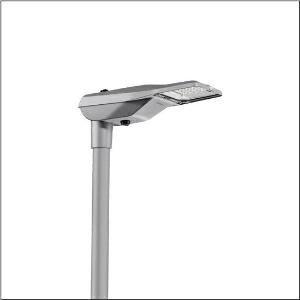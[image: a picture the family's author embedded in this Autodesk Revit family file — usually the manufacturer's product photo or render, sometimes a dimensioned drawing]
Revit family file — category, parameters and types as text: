
# Revit family: streetlight_sl_21_iq_micro___st1_0a_5xe1d21y08db_e1fc
name_source: partatom
category: Lighting Fixtures
units: mm (PartAtom-declared; Revit-internal decimal feet)

## family parameters
Cut with Voids When Loaded = No
Host = Face
Light Source = No
Part Type = Normal
Room Calculation Point = No
Round Connector Dimension = Use Diameter
Shared = No

## types (1)
- --- (1 x LED, 4100 lm, 39.1 W, 2200K)
    Apparent Load = 39 VA
    CIE Flux Codes = 37 72 97 100 100
    Color Rendering = 70
    Color Temperature = 2200K
    Default Elevation = 1800 mm
    Description = Streetlight SL 21 iQ micro, mast luminaire, primary light control with lens, of PMMA, primary optical cover: cover, of toughened safety glass, transparent, light distribution: ST1.0a, light emission: direct distribution, primary light characteristic: asymmetric, installation type: post-top, side-entry, LED, High Power LED, rated luminous flux: 4.100lm, luminous efficacy: 105lm/W, light colour: 722, colour temperature: 2200K, control: presetting dimming logarithmic, Street-Remote, Auto-Match, Temp-Guard, Lumen-Switch, Night-Set, Smart-Wire, Light-Fading, Desk-Remote (wireless, voltage-free reading and setting of iQ features in the workshop via application-optimized NFC function/RFID function), optimised constant luminous flux control (CLO 2.0), mains connection: 220..240V, AC, 50/60Hz, start of lifetime: 39W, end of service life: 41W, reduction: 17W, luminaire housing, of diecast aluminium, powder-coated, Siteco® metallic grey (DB 702S), corrosivity category C5 mid according to DIN EN ISO 12944, please order mast flange separately, inclination adjustable: 0°, 5°, 10°, 15°, sealing non-destructively replaceable, multi-level sealing system, length: 528mm, width: 235mm, height: 110mm, mast flange for spigot size: 42mm (side-entry): 5XC10008XM4, 60/48mm (side-entry/post-top): 5XC10108XM2, 76/60mm (side-entry/post-top): 5XC10108XM1, Smart Interface below and above, protection rating (complete): IP66, insulation class (complete): insulation class II (safety insulation), certification: CE, ENEC, ENEC+, VDE, impact resistance: IK09, permissible operating ambient temperature for outdoor applications: -40..+50°C, standard-compliant lighting for roads and squares, packaging unit: 1 piece

Light Distribution: ST1.0a
    Height = 110 mm
    Lamp = 1 x LED
    Lamp Light Flux = 4100 lm
    Lamp Power = 39.1 W
    Lamp count = 1
    Length = 528 mm
    Luminous efficacy = 105 lm/W
    Manufacturer = Siteco
    ModVariant = No
    Model = 5XE1D21Y08DB
    Number of Poles = 1
    OnlyDefault = Yes
    Power Factor = 1
    Product Name = Streetlight SL 21 iQ micro | ST1.0a
    Product group = mast luminaire | pylon top
    ProductGroupID = 6100
    Protection Class = Protection class II
    Protection Degree = IP 66
    RLX_Detail_Level = 1
    RLX_Emergency_Light_Flux = 0 lm
    RLX_Emergency_Type = 0
    RLX_Emergency_Type_DB = No
    RlxData = <blob elided: 98689 chars, md5=dc7b3f6a>
    Socket = socket
    Standby Power = 0 W
    System Light Flux = 4100 lm
    System Power = 39 W
    Type Comments = factory setting: luminous flux: 100 % | dim-lin: 254 | 765 mA
    Type Image = l_1007239.jpg
    URL = http://relux.com
    VarID = @adj_063767
    Voltage = 0 V
    Weight = 0.00 kg
    Width = 235 mm

## geometry (parser evidence)
native form markers: Blend x4, Sweep x12
no freeform markers — native parametric forms only
